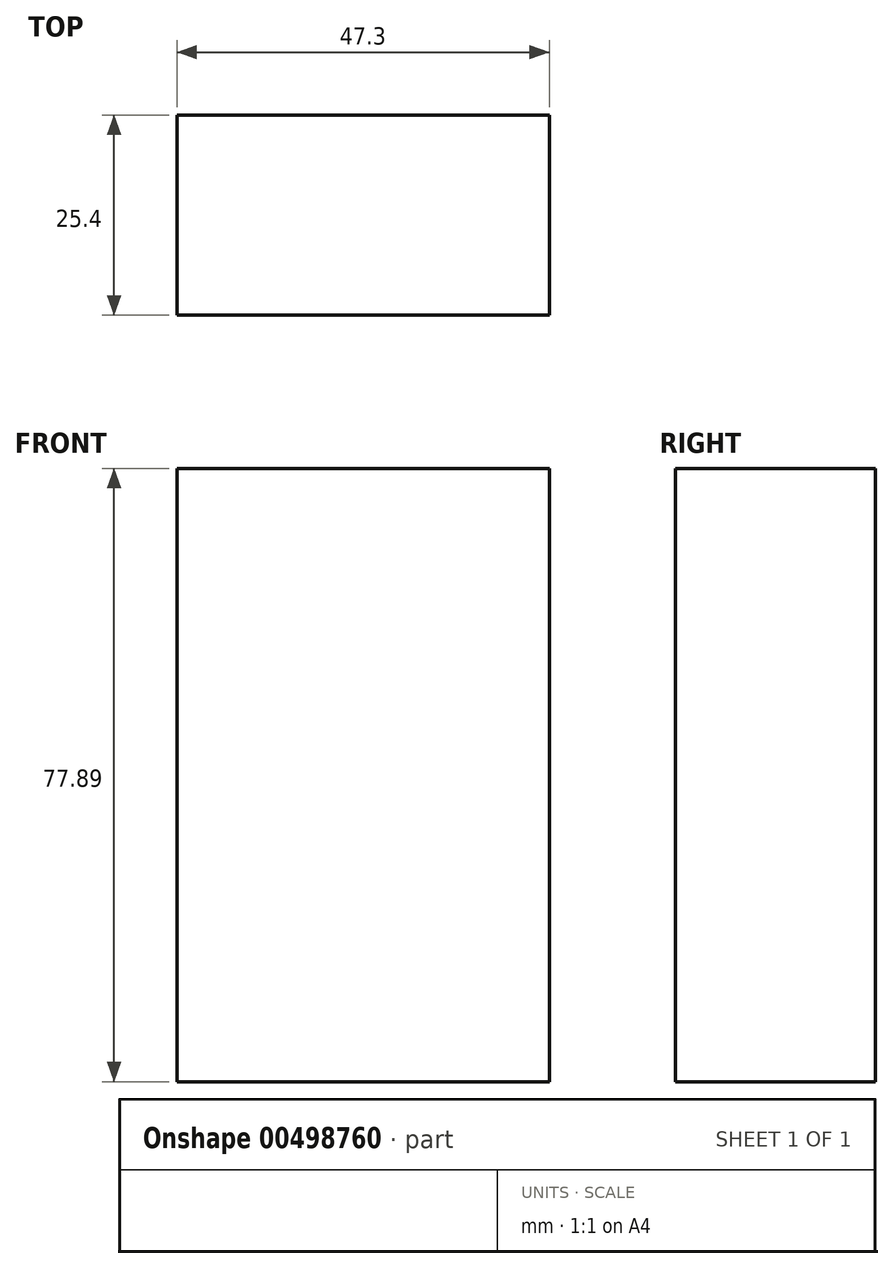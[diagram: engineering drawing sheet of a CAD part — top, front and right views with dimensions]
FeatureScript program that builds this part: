
annotation { "Feature Type Name" : "Feature", "Feature Type Description" : "" }
export const myFeature = defineFeature(function(context is Context, id is Id, definition is map)
    precondition{}
    {
        {
            var Q0;
            Q0=qCreatedBy(makeId("Front.planeOp"),FACE);
            var sketch = newSketch(context, id + "F0", { "sketchPlane" : qUnion([Q0])});
            skLineSegment(sketch, "E0.bottom", {"start": v(-102.78, 14.06) * mm, "end": v(-55.48, 14.06) * mm});
            skLineSegment(sketch, "E0.top", {"start": v(-102.78, -63.83) * mm, "end": v(-55.48, -63.83) * mm});
            skLineSegment(sketch, "E0.left", {"start": v(-102.78, 14.06) * mm, "end": v(-102.78, -63.83) * mm});
            skLineSegment(sketch, "E0.right", {"start": v(-55.48, 14.06) * mm, "end": v(-55.48, -63.83) * mm});
            skSolve(sketch);
        }
        {
            var Q0;
            Q0 = qSketchRegion(id + "F0", true);
            extrude(context, id + "F1", {"entities" : qUnion([Q0]), "depth" : 25.4 * mm});
        }
    });
